# Revit family: Приточно-вытяжная система с рециркуляцией с водяным нагервом, водяным охлаждением
name_source: partatom
category: Оборудование
units: mm (PartAtom-declared; Revit-internal decimal feet)

## family parameters
Всегда вертикально = Да
Классификация = Нет
На основе рабочей плоскости = Нет
Общий = Нет
При загрузке вырезать с полостями = Нет
Размер круглого соединителя = Использовать диаметр
Тип детали = Нормальный
Точка принадлежности помещению = Нет

## types (16) — shared parameters
ADSK_Напряжение = 380 В
ADSK_Свободный напор воздуха = 400.0 Па
Высота рамы = 120 мм
Длина гибкой встаки = 125 мм
Длина клапана FC = 120 мм
zero-valued in all types: Отметка по умолчанию

## per-type parameters (varying)
| type | ADSK_Размер_Высота | ADSK_Размер_Длина | ADSK_Размер_Ширина | ADSK_Частота вращения двигателя (приток) | Высота ГВ | Длина рамы | Ширина ГВ |
| 1А | 505 мм | 3225 мм | 980 мм | 2835 | 505 мм | 2855 мм | 980 мм |
| 2А | 505 мм | 3225 мм | 980 мм | 2830 | 505 мм | 2855 мм | 980 мм |
| 16B | 2580 мм | 5881 мм | 2580 мм | 1465 | 2580 мм | 5511 мм | 2580 мм |
| 3A | 695 мм | 3389 мм | 1080 мм | 2880 | 695 мм | 3019 мм | 1080 мм |
| 4A | 695 мм | 3389 мм | 1360 мм | 2880 | 695 мм | 3019 мм | 1360 мм |
| 5A | 803 мм | 3473 мм | 1360 мм | 2905 | 803 мм | 3103 мм | 1360 мм |
| 6A | 803 мм | 3973 мм | 1580 мм | 1455 | 803 мм | 3603 мм | 1580 мм |
| 7A | 990 мм | 3967 мм | 1580 мм | 2945 | 990 мм | 3597 мм | 1580 мм |
| 8A | 990 мм | 4067 мм | 1950 мм | 1455 | 990 мм | 3697 мм | 1950 мм |
| 9A | 1095 мм | 4149 мм | 2160 мм | 1455 | 1095 мм | 3779 мм | 2160 мм |
| 10B | 1360 мм | 4626 мм | 2040 мм | 1460 | 1360 мм | 4256 мм | 2040 мм |
| 12B | 1680 мм | 4860 мм | 2040 мм | 1465 | 1680 мм | 4490 мм | 2040 мм |
| 11B | 1360 мм | 4676 мм | 2580 мм | 1465 | 1360 мм | 4306 мм | 2580 мм |
| 13B | 2040 мм | 5204 мм | 2040 мм | 1465 | 2040 мм | 4834 мм | 2040 мм |
| 14B | 1680 мм | 5194 мм | 2580 мм | 1470 | 1680 мм | 4824 мм | 2580 мм |
| 15B | 2040 мм | 5374 мм | 2580 мм | 1460 | 2040 мм | 5004 мм | 2580 мм |
